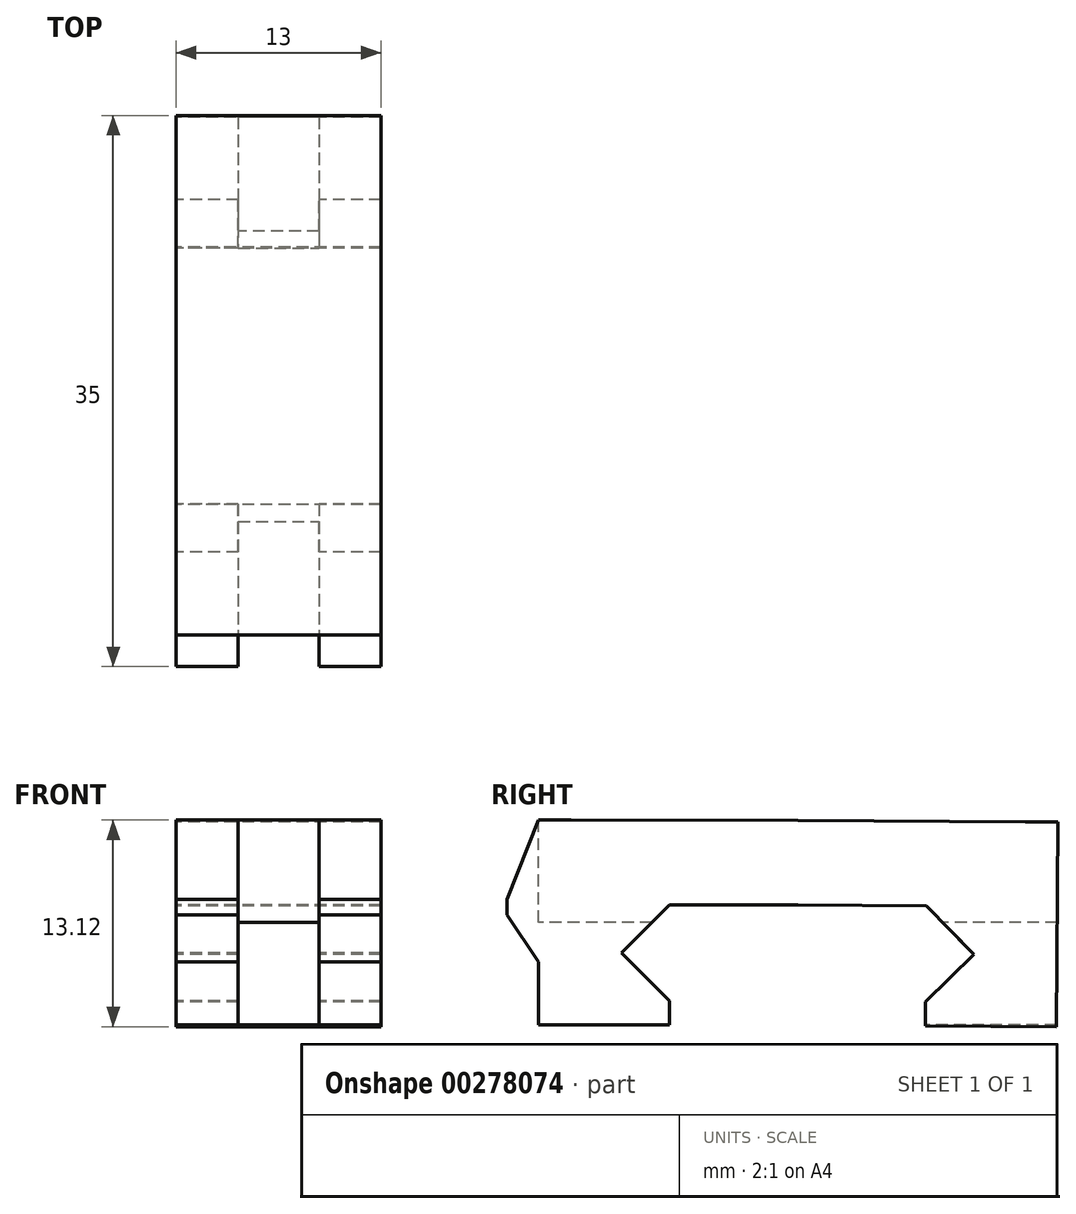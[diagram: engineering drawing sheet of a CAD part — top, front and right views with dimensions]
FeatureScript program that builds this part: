
annotation { "Feature Type Name" : "Feature", "Feature Type Description" : "" }
export const myFeature = defineFeature(function(context is Context, id is Id, definition is map)
    precondition{}
    {
        {
            var Q0;
            Q0=qCreatedBy(makeId("Right.planeOp"),FACE);
            var sketch = newSketch(context, id + "F0", { "sketchPlane" : qUnion([Q0])});
            skLineSegment(sketch, "E0", {"start": v(-28.67, -6.5) * mm, "end": v(-28.67, -4.97) * mm});
            skLineSegment(sketch, "E1", {"start": v(-28.67, -4.97) * mm, "end": v(-31.72, -1.94) * mm});
            skLineSegment(sketch, "E2", {"start": v(-31.72, -1.94) * mm, "end": v(-28.69, 1.1) * mm});
            skLineSegment(sketch, "E3", {"start": v(-34.94, 6.5) * mm, "end": v(-37, 1.47) * mm});
            skLineSegment(sketch, "E4", {"start": v(-37, 1.47) * mm, "end": v(-37, -6.5) * mm});
            skLineSegment(sketch, "E5", {"start": v(-37, -6.5) * mm, "end": v(-28.67, -6.5) * mm});
            skLineSegment(sketch, "E6", {"start": v(-34.94, 6.5) * mm, "end": v(-37, 6.5) * mm});
            skLineSegment(sketch, "E7", {"start": v(-37, 6.5) * mm, "end": v(-37, 1.47) * mm});
            skLineSegment(sketch, "E8", {"start": v(-20.52, 1.1) * mm, "end": v(-20.5, 6.47) * mm});
            skLineSegment(sketch, "E9", {"start": v(-20.52, 1.1) * mm, "end": v(-28.69, 1.1) * mm});
            skLineSegment(sketch, "E10", {"start": v(-20.5, 6.47) * mm, "end": v(-34.94, 6.5) * mm});
            skLineSegment(sketch, "E11", {"start": v(-37, 1.47) * mm, "end": v(-39, 1.47) * mm});
            skLineSegment(sketch, "E12", {"start": v(-39, 1.47) * mm, "end": v(-39, 0.47) * mm});
            skLineSegment(sketch, "E13", {"start": v(-39, 0.47) * mm, "end": v(-37, -2.51) * mm});
            skLineSegment(sketch, "E14", {"start": v(-37, 6.5) * mm, "end": v(-39, 1.47) * mm});
            skSolve(sketch);
        }
        {
            var Q0;
            Q0=makeQuery(id+"F0.imprint","IMPRINT",FACE,{"disambiguationData":[TD([[makeQuery(id+"F0.imprint","IMPRINT",EDGE,{"derivedFrom":sQuery(id+"F0.wireOp",EDGE,"E0")}),1.0]])]});
            var Q1;
            Q1=makeQuery(id+"F0.imprint","IMPRINT",FACE,{"disambiguationData":[TD([[makeQuery(id+"F0.imprint","IMPRINT",EDGE,{"derivedFrom":sQuery(id+"F0.wireOp",EDGE,"E3")}),-1.0]])]});
            extrude(context, id + "F1", {"entities" : qUnion([Q0, Q1]), "depth" : 13 * mm});
        }
        {
            var Q0;
            Q0=makeQuery(id+"F1.opExtrude","SWEPT_FACE",FACE,{"disambiguationData":[OSD([sQuery(id+"F0.wireOp",EDGE,"E4")])]});
            var sketch = newSketch(context, id + "F2", { "sketchPlane" : qUnion([Q0])});
            skLineSegment(sketch, "E15", {"start": v(0, 6.5) * mm, "end": v(13, 6.5) * mm});
            skLineSegment(sketch, "E16", {"start": v(13, 6.5) * mm, "end": v(13, -6.5) * mm});
            skLineSegment(sketch, "E17", {"start": v(13, -6.5) * mm, "end": v(0, -6.5) * mm});
            skLineSegment(sketch, "E18", {"start": v(0, -6.5) * mm, "end": v(0, 6.5) * mm});
            skLineSegment(sketch, "E19", {"start": v(6.5, 6.5) * mm, "end": v(6.5, -6.5) * mm});
            skCircle(sketch, "E20", {"center": v(6.5, 0) * mm, "radius": 2.58 * mm});
            skLineSegment(sketch, "E21", {"start": v(3.93, 0) * mm, "end": v(9.07, 0) * mm});
            skLineSegment(sketch, "E22", {"start": v(9.07, 0) * mm, "end": v(13, 0) * mm});
            skLineSegment(sketch, "E23", {"start": v(9.07, 0) * mm, "end": v(9.07, 6.5) * mm});
            skLineSegment(sketch, "E24", {"start": v(9.07, 6.5) * mm, "end": v(3.93, 6.5) * mm});
            skLineSegment(sketch, "E25", {"start": v(3.93, 6.5) * mm, "end": v(3.93, 0) * mm});
            skLineSegment(sketch, "E26", {"start": v(3.93, 0) * mm, "end": v(3.93, -6.5) * mm});
            skLineSegment(sketch, "E27", {"start": v(3.93, -6.5) * mm, "end": v(9.07, -6.5) * mm});
            skLineSegment(sketch, "E28", {"start": v(9.07, -6.5) * mm, "end": v(9.07, 0) * mm});
            skSolve(sketch);
        }
        {
            var Q0;
            Q0=makeQuery(id+"F1.opExtrude","SWEPT_BODY",BODY,{"disambiguationData":[OSD([sQuery(id+"F0.wireOp",EDGE,"E0"),sQuery(id+"F0.wireOp",EDGE,"E1"),sQuery(id+"F0.wireOp",EDGE,"E2"),sQuery(id+"F0.wireOp",EDGE,"E4"),sQuery(id+"F0.wireOp",EDGE,"E5"),sQuery(id+"F0.wireOp",EDGE,"E6"),sQuery(id+"F0.wireOp",EDGE,"E7"),sQuery(id+"F0.wireOp",EDGE,"E8"),sQuery(id+"F0.wireOp",EDGE,"E9"),sQuery(id+"F0.wireOp",EDGE,"E10")])]});
            var Q1;
            Q1=makeQuery(id+"F1.opExtrude","SWEPT_FACE",FACE,{"disambiguationData":[OSD([sQuery(id+"F0.wireOp",EDGE,"E8")])]});
            mirror(context, id + "F3", {"operationType" : NewBodyOperationType.ADD, "entities" : qUnion([Q0]), "mirrorPlane" : qUnion([Q1])});
        }
        {
            var Q0;
            {var subQ0=sQuery(id+"F2.wireOp",EDGE,"E20");var subQ1=sQuery(id+"F2.wireOp",EDGE,"E19");var subQ2=makeQuery(id+"F2.imprint","INTERSECT",VERTEX,{"disambiguationData":[OD(0.0)],"derivedFrom":[subQ1,subQ0]});Q0=makeQuery(id+"F2.imprint","IMPRINT",FACE,{"disambiguationData":[TD([[makeQuery(id+"F2.imprint","IMPRINT",EDGE,{"disambiguationData":[TD([[subQ2,-1.0]])],"derivedFrom":subQ1}),1.0]])]});}
            var Q1;
            {var subQ0=sQuery(id+"F2.wireOp",EDGE,"E20");var subQ1=sQuery(id+"F2.wireOp",EDGE,"E19");var subQ2=makeQuery(id+"F2.imprint","INTERSECT",VERTEX,{"disambiguationData":[OD(0.0)],"derivedFrom":[subQ1,subQ0]});Q1=makeQuery(id+"F2.imprint","IMPRINT",FACE,{"disambiguationData":[TD([[makeQuery(id+"F2.imprint","IMPRINT",EDGE,{"disambiguationData":[TD([[subQ2,-1.0]])],"derivedFrom":subQ1}),-1.0]])]});}
            var Q2;
            {var subQ0=sQuery(id+"F2.wireOp",EDGE,"E21");var subQ1=sQuery(id+"F2.wireOp",EDGE,"E19");var subQ2=makeQuery(id+"F2.imprint","INTERSECT",VERTEX,{"derivedFrom":[subQ1,subQ0]});Q2=makeQuery(id+"F2.imprint","IMPRINT",FACE,{"disambiguationData":[TD([[makeQuery(id+"F2.imprint","IMPRINT",EDGE,{"disambiguationData":[TD([[subQ2,-1.0]])],"derivedFrom":subQ1}),-1.0]])]});}
            var Q3;
            {var subQ0=sQuery(id+"F2.wireOp",EDGE,"E21");var subQ1=sQuery(id+"F2.wireOp",EDGE,"E19");var subQ2=makeQuery(id+"F2.imprint","INTERSECT",VERTEX,{"derivedFrom":[subQ1,subQ0]});Q3=makeQuery(id+"F2.imprint","IMPRINT",FACE,{"disambiguationData":[TD([[makeQuery(id+"F2.imprint","IMPRINT",EDGE,{"disambiguationData":[TD([[subQ2,-1.0]])],"derivedFrom":subQ1}),1.0]])]});}
            extrude(context, id + "F4", {"entities" : qUnion([Q0, Q1, Q2, Q3]), "operationType" : NewBodyOperationType.REMOVE, "oppositeDirection" : true, "depth" : 34.5 * mm});
        }
        {
            var Q0;
            {var subQ0=sQuery(id+"F0.wireOp",EDGE,"E11");Q0=makeQuery(id+"F0.imprint","IMPRINT",FACE,{"disambiguationData":[TD([[makeQuery(id+"F0.imprint","IMPRINT",EDGE,{"derivedFrom":subQ0}),1.0]])]});}
            var Q1;
            Q1=makeQuery(id+"F0.imprint","IMPRINT",FACE,{"disambiguationData":[TD([[makeQuery(id+"F0.imprint","IMPRINT",EDGE,{"derivedFrom":sQuery(id+"F0.wireOp",EDGE,"E7")}),-1.0]])]});
            extrude(context, id + "F5", {"entities" : qUnion([Q0, Q1]), "operationType" : NewBodyOperationType.ADD, "depth" : 13 * mm});
        }
        {
            var Q0;
            {var subQ0=sQuery(id+"F2.wireOp",EDGE,"E20");var subQ1=sQuery(id+"F2.wireOp",EDGE,"E19");var subQ2=makeQuery(id+"F2.imprint","INTERSECT",VERTEX,{"disambiguationData":[OD(0.0)],"derivedFrom":[subQ1,subQ0]});Q0=makeQuery(id+"F2.imprint","IMPRINT",FACE,{"disambiguationData":[TD([[makeQuery(id+"F2.imprint","IMPRINT",EDGE,{"disambiguationData":[TD([[subQ2,-1.0]])],"derivedFrom":subQ1}),1.0]])]});}
            var Q1;
            {var subQ0=sQuery(id+"F2.wireOp",EDGE,"E20");var subQ1=sQuery(id+"F2.wireOp",EDGE,"E19");var subQ2=makeQuery(id+"F2.imprint","INTERSECT",VERTEX,{"disambiguationData":[OD(0.0)],"derivedFrom":[subQ1,subQ0]});Q1=makeQuery(id+"F2.imprint","IMPRINT",FACE,{"disambiguationData":[TD([[makeQuery(id+"F2.imprint","IMPRINT",EDGE,{"disambiguationData":[TD([[subQ2,-1.0]])],"derivedFrom":subQ1}),-1.0]])]});}
            var Q2;
            {var subQ0=sQuery(id+"F2.wireOp",EDGE,"E21");var subQ1=sQuery(id+"F2.wireOp",EDGE,"E19");var subQ2=makeQuery(id+"F2.imprint","INTERSECT",VERTEX,{"derivedFrom":[subQ1,subQ0]});Q2=makeQuery(id+"F2.imprint","IMPRINT",FACE,{"disambiguationData":[TD([[makeQuery(id+"F2.imprint","IMPRINT",EDGE,{"disambiguationData":[TD([[subQ2,-1.0]])],"derivedFrom":subQ1}),-1.0]])]});}
            var Q3;
            {var subQ0=sQuery(id+"F2.wireOp",EDGE,"E21");var subQ1=sQuery(id+"F2.wireOp",EDGE,"E19");var subQ2=makeQuery(id+"F2.imprint","INTERSECT",VERTEX,{"derivedFrom":[subQ1,subQ0]});Q3=makeQuery(id+"F2.imprint","IMPRINT",FACE,{"disambiguationData":[TD([[makeQuery(id+"F2.imprint","IMPRINT",EDGE,{"disambiguationData":[TD([[subQ2,-1.0]])],"derivedFrom":subQ1}),1.0]])]});}
            extrude(context, id + "F6", {"entities" : qUnion([Q0, Q1, Q2, Q3]), "operationType" : NewBodyOperationType.REMOVE, "depth" : 15.6 * mm});
        }
        {
            var Q0;
            {var subQ5=sQuery(id+"F2.wireOp",EDGE,"E25");Q0=makeQuery(id+"F2.imprint","IMPRINT",FACE,{"disambiguationData":[TD([[makeQuery(id+"F2.imprint","IMPRINT",EDGE,{"derivedFrom":subQ5}),1.0]])]});}
            var Q1;
            {var subQ5=sQuery(id+"F2.wireOp",EDGE,"E23");Q1=makeQuery(id+"F2.imprint","IMPRINT",FACE,{"disambiguationData":[TD([[makeQuery(id+"F2.imprint","IMPRINT",EDGE,{"derivedFrom":subQ5}),1.0]])]});}
            var Q2;
            {var subQ5=sQuery(id+"F2.wireOp",EDGE,"E28");Q2=makeQuery(id+"F2.imprint","IMPRINT",FACE,{"disambiguationData":[TD([[makeQuery(id+"F2.imprint","IMPRINT",EDGE,{"derivedFrom":subQ5}),1.0]])]});}
            var Q3;
            {var subQ5=sQuery(id+"F2.wireOp",EDGE,"E26");Q3=makeQuery(id+"F2.imprint","IMPRINT",FACE,{"disambiguationData":[TD([[makeQuery(id+"F2.imprint","IMPRINT",EDGE,{"derivedFrom":subQ5}),1.0]])]});}
            extrude(context, id + "F7", {"entities" : qUnion([Q0, Q1, Q2, Q3]), "operationType" : NewBodyOperationType.REMOVE, "depth" : 5 * mm});
        }
    });
